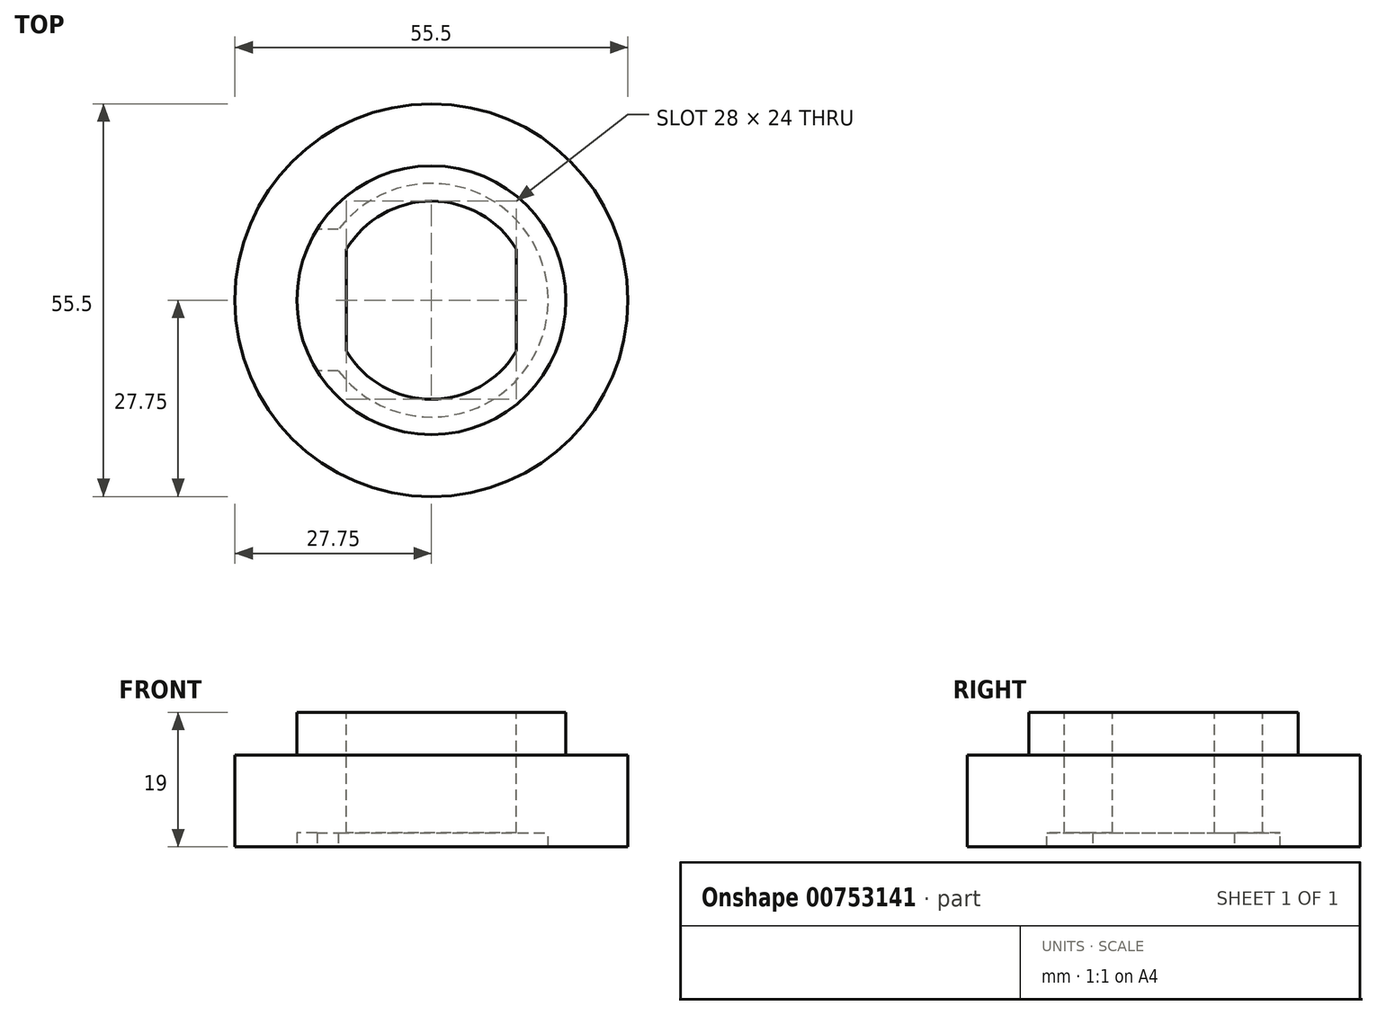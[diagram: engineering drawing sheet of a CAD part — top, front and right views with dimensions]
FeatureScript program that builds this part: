
annotation { "Feature Type Name" : "Feature", "Feature Type Description" : "" }
export const myFeature = defineFeature(function(context is Context, id is Id, definition is map)
    precondition{}
    {
        {
            var Q0;
            Q0=qCreatedBy(makeId("Front.planeOp"),FACE);
            var sketch = newSketch(context, id + "F0", { "sketchPlane" : qUnion([Q0])});
            skLineSegment(sketch, "E0", {"start": v(0, 25.58) * mm, "end": v(0, -23.97) * mm, "construction": true});
            skLineSegment(sketch, "E1", {"start": v(0, 0) * mm, "end": v(19, 0) * mm});
            skLineSegment(sketch, "E2", {"start": v(19, 0) * mm, "end": v(19, -6) * mm});
            skLineSegment(sketch, "E3", {"start": v(19, -6) * mm, "end": v(27.75, -6) * mm});
            skLineSegment(sketch, "E4", {"start": v(27.75, -6) * mm, "end": v(27.75, -19) * mm});
            skLineSegment(sketch, "E5", {"start": v(27.75, -19) * mm, "end": v(16.5, -19) * mm});
            skLineSegment(sketch, "E6", {"start": v(16.5, -19) * mm, "end": v(16.5, -17) * mm});
            skLineSegment(sketch, "E7", {"start": v(16.5, -17) * mm, "end": v(0, -17) * mm});
            skLineSegment(sketch, "E8", {"start": v(0, -17) * mm, "end": v(0, 0) * mm});
            skSolve(sketch);
        }
        {
            var Q0;
            Q0 = qSketchRegion(id + "F0", true);
            var Q1;
            Q1=sQuery(id+"F0.wireOp",EDGE,"E0");
            revolve(context, id + "F1", {"surfaceOperationType" : NewSurfaceOperationType.NEW, "entities" : qUnion([Q0]), "axis" : qUnion([Q1]), "revolveType" : RevolveType.FULL});
        }
        {
            var Q0;
            Q0=makeQuery(id+"F1.opRevolve","SWEPT_FACE",FACE,{"disambiguationData":[OSD([sQuery(id+"F0.wireOp",EDGE,"E1")])]});
            var sketch = newSketch(context, id + "F2", { "sketchPlane" : qUnion([Q0])});
            skArc(sketch, "E9", {"start": v(-12, -7.21) * mm, "mid": v(0, -14) * mm, "end": v(12, -7.21) * mm});
            skLineSegment(sketch, "E10", {"start": v(-12, 7.21) * mm, "end": v(-12, -7.21) * mm});
            skLineSegment(sketch, "E11", {"start": v(12, 7.21) * mm, "end": v(12, -7.21) * mm});
            skArc(sketch, "E12.trimOffspring", {"start": v(12, 7.21) * mm, "mid": v(0, 14) * mm, "end": v(-12, 7.21) * mm});
            skSolve(sketch);
        }
        {
            var Q0;
            Q0=makeQuery(id+"F2.imprint","IMPRINT",FACE,{"disambiguationData":[TD([[makeQuery(id+"F2.imprint","IMPRINT",EDGE,{"derivedFrom":sQuery(id+"F2.wireOp",EDGE,"E9")}),1.0]])]});
            extrude(context, id + "F3", {"entities" : qUnion([Q0]), "operationType" : NewBodyOperationType.REMOVE, "oppositeDirection" : true, "depth" : 25 * mm, "offsetDistance" : 25 * mm});
        }
        {
            var Q0;
            Q0=makeQuery(id+"F1.opRevolve","SWEPT_FACE",FACE,{"disambiguationData":[OSD([sQuery(id+"F0.wireOp",EDGE,"E5")])]});
            var sketch = newSketch(context, id + "F4", { "sketchPlane" : qUnion([Q0])});
            skArc(sketch, "E13", {"start": v(-16.16, 10) * mm, "mid": v(-19, 0) * mm, "end": v(-16.16, -10) * mm});
            skLineSegment(sketch, "E14", {"start": v(0, -10) * mm, "end": v(-16.16, -10) * mm});
            skLineSegment(sketch, "E15", {"start": v(0, 10) * mm, "end": v(-16.16, 10) * mm});
            skLineSegment(sketch, "E16", {"start": v(0, -10) * mm, "end": v(0, 10) * mm});
            skSolve(sketch);
        }
        {
            var Q0;
            {var subQ0=sQuery(id+"F4.wireOp",EDGE,"E13");Q0=makeQuery(id+"F4.imprint","IMPRINT",FACE,{"disambiguationData":[TD([[makeQuery(id+"F4.imprint","IMPRINT",EDGE,{"derivedFrom":subQ0}),1.0]])]});}
            var Q1;
            Q1=makeQuery(id+"F1.opRevolve","SWEPT_FACE",FACE,{"disambiguationData":[OSD([sQuery(id+"F0.wireOp",EDGE,"E7")])]});
            extrude(context, id + "F5", {"entities" : qUnion([Q0]), "operationType" : NewBodyOperationType.REMOVE, "endBound" : BoundingType.UP_TO_SURFACE, "oppositeDirection" : true, "depth" : 25 * mm, "endBoundEntityFace" : qUnion([Q1]), "offsetDistance" : 25 * mm});
        }
    });
